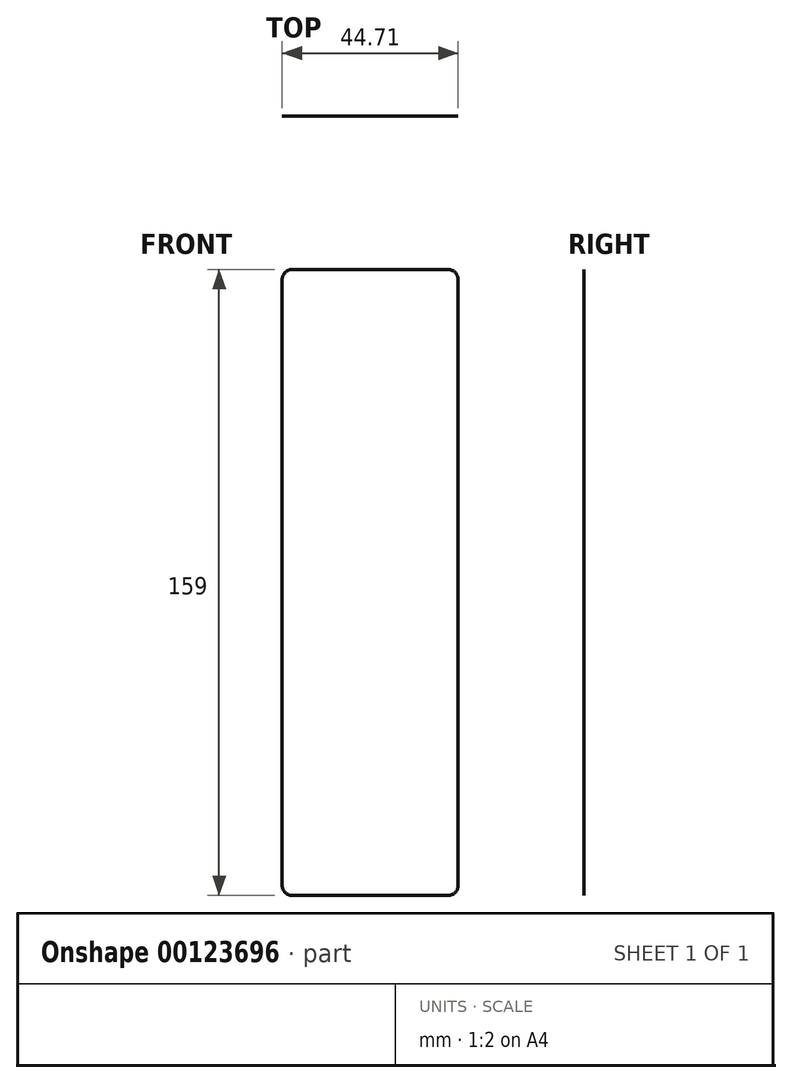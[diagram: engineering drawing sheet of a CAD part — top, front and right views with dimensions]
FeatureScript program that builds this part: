
annotation { "Feature Type Name" : "Feature", "Feature Type Description" : "" }
export const myFeature = defineFeature(function(context is Context, id is Id, definition is map)
    precondition{}
    {
        {
            var Q0;
            Q0=qCreatedBy(makeId("Front.planeOp"),FACE);
            var sketch = newSketch(context, id + "F0", { "sketchPlane" : qUnion([Q0])});
            skLineSegment(sketch, "E0.bottom", {"start": v(-18.13, 94.88) * mm, "end": v(21.5, 94.88) * mm});
            skLineSegment(sketch, "E0.top", {"start": v(-18.13, -64.12) * mm, "end": v(21.5, -64.12) * mm});
            skLineSegment(sketch, "E0.left", {"start": v(-20.67, 92.34) * mm, "end": v(-20.67, -61.58) * mm});
            skLineSegment(sketch, "E0.right", {"start": v(24.04, 92.34) * mm, "end": v(24.04, -61.58) * mm});
            skPoint(sketch, "E1.visualSharp", {"position": v(-20.67, 94.88) * mm});
            skArc(sketch, "E1.filletArc", {"start": v(-18.13, 94.88) * mm, "mid": v(-19.92, 94.14) * mm, "end": v(-20.67, 92.34) * mm});
            skPoint(sketch, "E2.visualSharp", {"position": v(24.04, 94.88) * mm});
            skArc(sketch, "E2.filletArc", {"start": v(24.04, 92.34) * mm, "mid": v(23.3, 94.14) * mm, "end": v(21.5, 94.88) * mm});
            skPoint(sketch, "E3.visualSharp", {"position": v(24.04, -64.12) * mm});
            skArc(sketch, "E3.filletArc", {"start": v(21.5, -64.12) * mm, "mid": v(23.3, -63.38) * mm, "end": v(24.04, -61.58) * mm});
            skPoint(sketch, "E4.visualSharp", {"position": v(-20.67, -64.12) * mm});
            skArc(sketch, "E4.filletArc", {"start": v(-20.67, -61.58) * mm, "mid": v(-19.92, -63.38) * mm, "end": v(-18.13, -64.12) * mm});
            skSolve(sketch);
        }
        {
            var Q0;
            Q0 = qSketchRegion(id + "F0", true);
            extrude(context, id + "F1", {"entities" : qUnion([Q0]), "depth" : 1 / 203.2 * mm});
        }
    });
